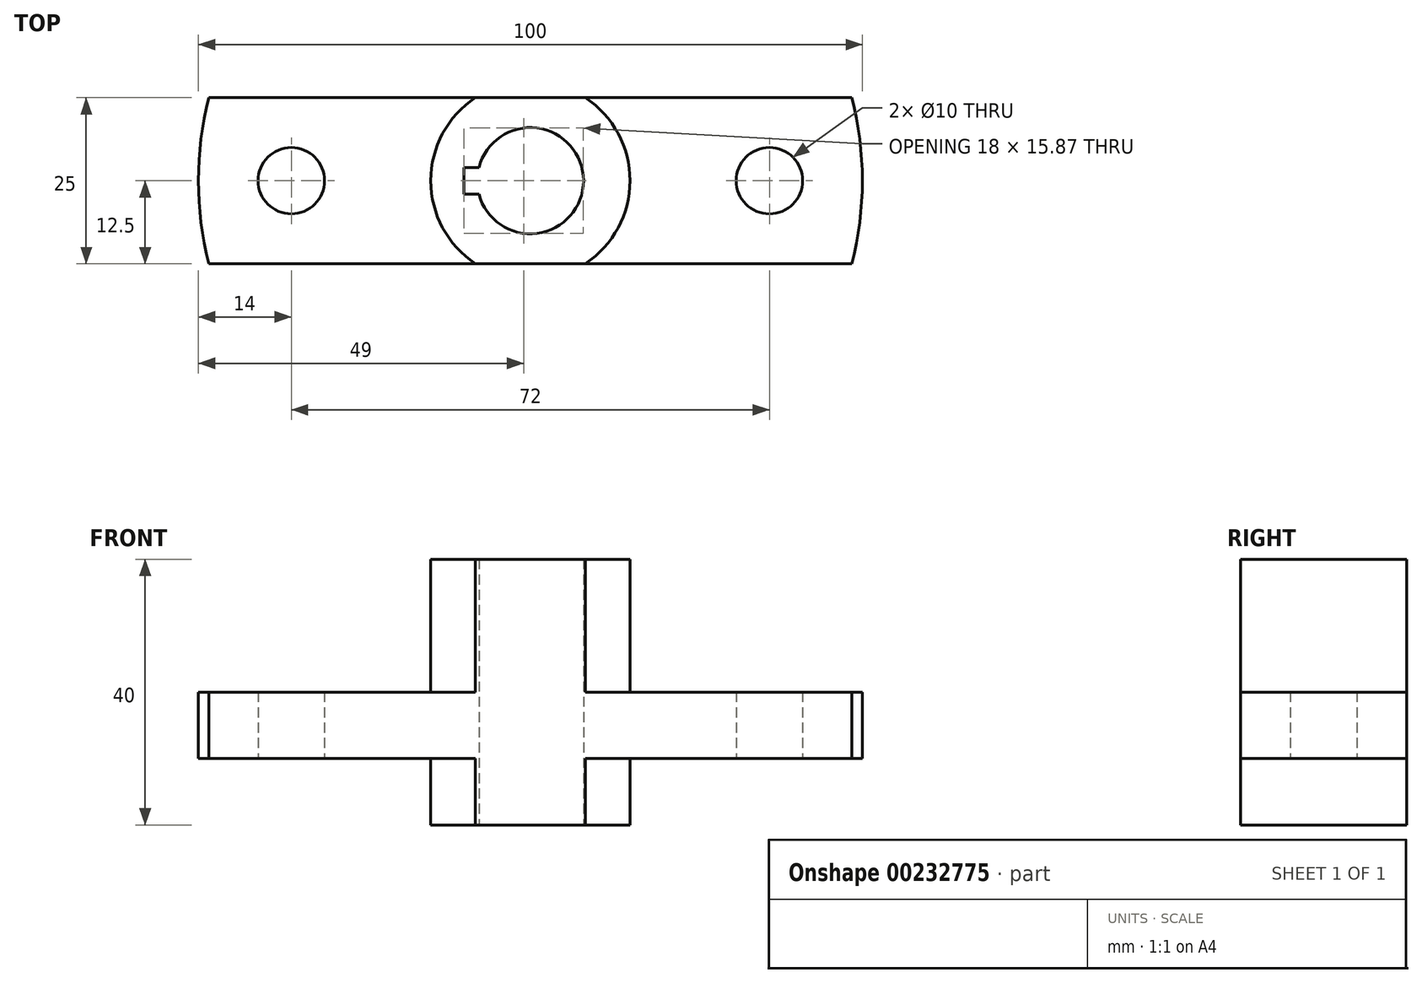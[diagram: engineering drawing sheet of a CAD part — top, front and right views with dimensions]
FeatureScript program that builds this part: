
annotation { "Feature Type Name" : "Feature", "Feature Type Description" : "" }
export const myFeature = defineFeature(function(context is Context, id is Id, definition is map)
    precondition{}
    {
        {
            var Q0;
            Q0=qCreatedBy(makeId("Top.planeOp"),FACE);
            var sketch = newSketch(context, id + "F0", { "sketchPlane" : qUnion([Q0])});
            skArc(sketch, "E0", {"start": v(-7.75, -2) * mm, "mid": v(8, 0) * mm, "end": v(-7.75, 2) * mm});
            skArc(sketch, "E1", {"start": v(-8.3, 12.5) * mm, "mid": v(-15, 0) * mm, "end": v(-8.3, -12.5) * mm});
            skArc(sketch, "E2", {"start": v(-48.41, 12.5) * mm, "mid": v(-50, 0) * mm, "end": v(-48.41, -12.5) * mm});
            skLineSegment(sketch, "E3.bottom", {"start": v(48.41, 12.5) * mm, "end": v(-48.41, 12.5) * mm});
            skLineSegment(sketch, "E3.top", {"start": v(48.41, -12.5) * mm, "end": v(-48.41, -12.5) * mm});
            skPoint(sketch, "E3.right.end.orphan", {"position": v(-40.1, -12.5) * mm});
            skPoint(sketch, "E3.right.start.orphan", {"position": v(-40.1, 12.5) * mm});
            skPoint(sketch, "E3.left.start.orphan", {"position": v(40.1, 12.5) * mm});
            skArc(sketch, "E4.trimOffspring", {"start": v(48.41, -12.5) * mm, "mid": v(50, 0) * mm, "end": v(48.41, 12.5) * mm});
            skPoint(sketch, "E5.orphan", {"position": v(40.1, -12.5) * mm});
            skLineSegment(sketch, "E6.bottom", {"start": v(-7.75, 2) * mm, "end": v(-10, 2) * mm});
            skLineSegment(sketch, "E6.top", {"start": v(-7.75, -2) * mm, "end": v(-10, -2) * mm});
            skLineSegment(sketch, "E6.right", {"start": v(-10, 2) * mm, "end": v(-10, -2) * mm});
            skPoint(sketch, "E6.middle", {"position": v(-8, 0) * mm});
            skPoint(sketch, "E6.left.start.orphan", {"position": v(-6, 2) * mm});
            skPoint(sketch, "E7.orphan", {"position": v(-6, -2) * mm});
            skCircle(sketch, "E8", {"center": v(36, 0) * mm, "radius": 5 * mm});
            skCircle(sketch, "E9", {"center": v(-36, 0) * mm, "radius": 5 * mm});
            skArc(sketch, "E10.trimOffspring", {"start": v(8.3, -12.5) * mm, "mid": v(15, 0) * mm, "end": v(8.3, 12.5) * mm});
            skSolve(sketch);
        }
        {
            var Q0;
            Q0=makeQuery(id+"F0.imprint","IMPRINT",FACE,{"disambiguationData":[TD([[makeQuery(id+"F0.imprint","IMPRINT",EDGE,{"derivedFrom":sQuery(id+"F0.wireOp",EDGE,"E0")}),-1.0]])]});
            extrude(context, id + "F1", {"entities" : qUnion([Q0]), "depth" : 30 * mm, "hasSecondDirection" : true, "secondDirectionOppositeDirection" : true, "secondDirectionDepth" : 10 * mm});
        }
        {
            var Q0;
            {var subQ1=sQuery(id+"F0.wireOp",EDGE,"E1");Q0=makeQuery(id+"F0.imprint","IMPRINT",FACE,{"disambiguationData":[TD([[makeQuery(id+"F0.imprint","IMPRINT",EDGE,{"derivedFrom":subQ1}),-1.0]])]});}
            var Q1;
            {var subQ0=sQuery(id+"F0.wireOp",EDGE,"E4.trimOffspring");Q1=makeQuery(id+"F0.imprint","IMPRINT",FACE,{"disambiguationData":[TD([[makeQuery(id+"F0.imprint","IMPRINT",EDGE,{"derivedFrom":subQ0}),1.0]])]});}
            extrude(context, id + "F2", {"entities" : qUnion([Q0, Q1]), "operationType" : NewBodyOperationType.ADD, "depth" : 10 * mm});
        }
    });
